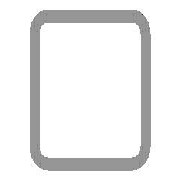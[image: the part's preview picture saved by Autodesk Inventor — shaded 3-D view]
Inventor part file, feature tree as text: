
AUTODESK INVENTOR PART (.ipt)
format: ipt  version: 2016 (Build 200138000, 138)  size: 133,120 bytes
history: native  units: mm (DEFAULTED — no unit token found)
features: other x4, sketch x3, plane x2, split x1
ambient origin geometry x8: Origin, YZ Plane, XZ Plane, XY Plane, X Axis, Y Axis, Z Axis, Center Point
bodies: Solid1 (feature_tree), Body (feature_tree)
feature tree (10):
  parser-record x1  (decoder bookkeeping rows leaked as tree rows — omitted from the tree; the rows remain in map.json)
  other  "Driven Length"
  other  "Start plane"
  other  "End plane"
  plane  "Work Plane4"
  split  "Split1"
  sketch  "Sketch"  dims[d7=4.0mm d9=25.0mm d11=25.0mm d12=2.0mm d13=-0.0mm d14=275.0mm d15=12.5mm d16=12.5mm d17=90.0deg d18=275.0mm]
  sketch  "Sketch3"  dims[d3=275.0mm]
  plane  "Work Plane3"
  sketch  "Sketch4"  dims[d4=0.0mm]
